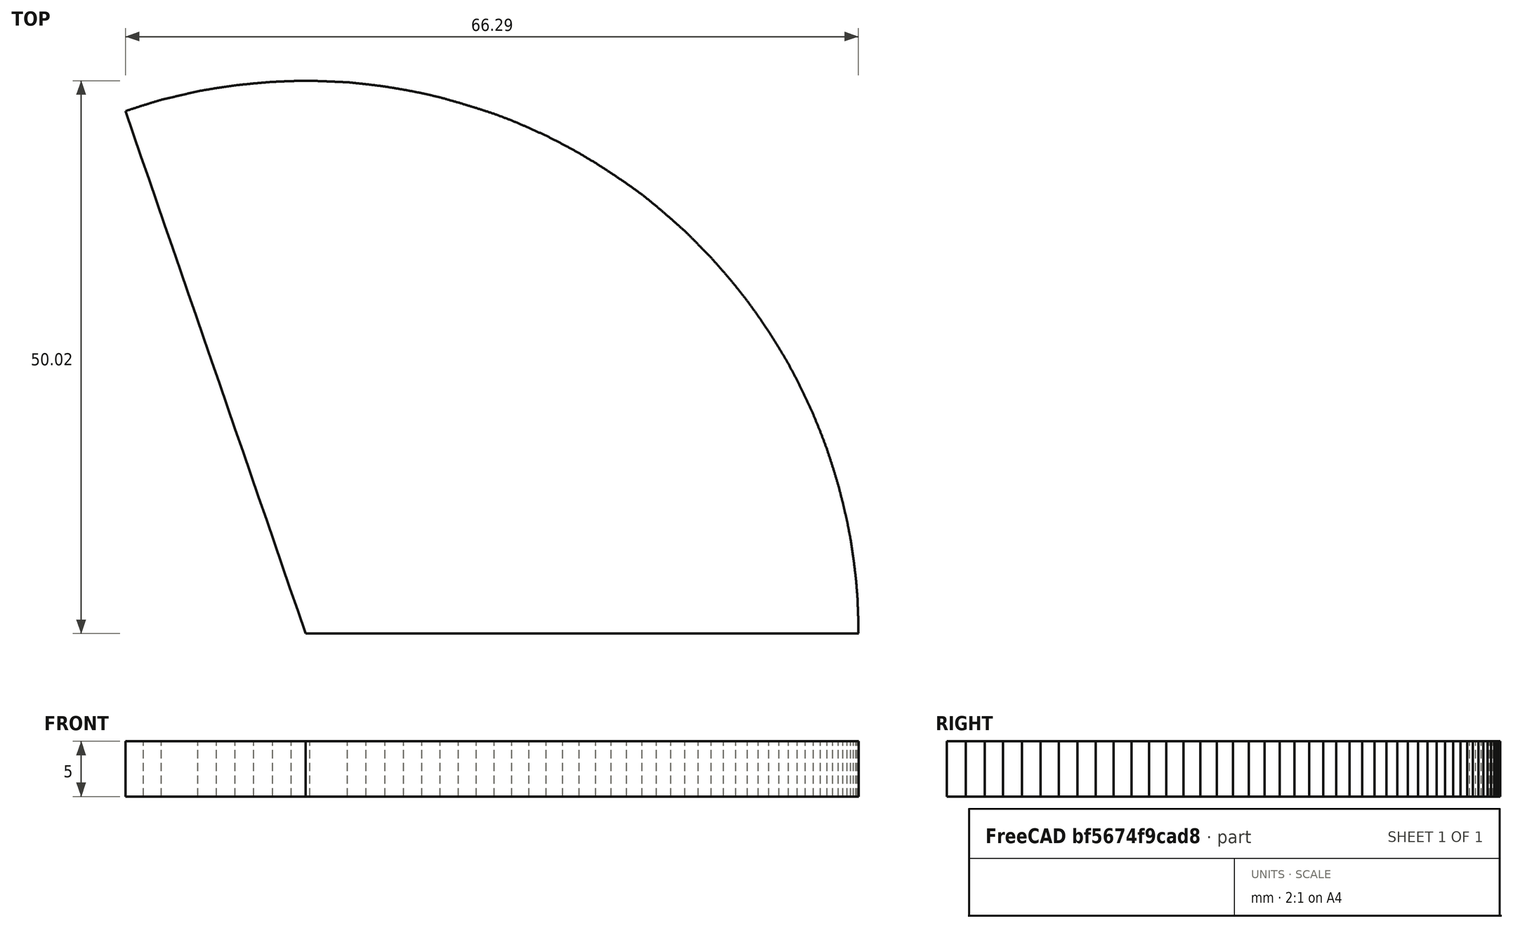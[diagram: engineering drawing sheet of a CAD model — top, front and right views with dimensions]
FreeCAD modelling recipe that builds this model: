
FCSTD DOCUMENT  (FreeCAD 0.19R)
Label: F-35_v2_parts_19
License: All rights reserved
LicenseURL: http://en.wikipedia.org/wiki/All_rights_reserved
objects: App::DocumentObjectGroup×2, PartDesign::CoordinateSystem×1, App::FeaturePython×1, Sketcher::SketchObject×1, PartDesign::Pad×1, PartDesign::Body×1, App::Part×1
note: 5 computed .brp shape members not serialized (recipe doc carries the construction recipe); baked Part::Feature solids carry a one-line shape summary decoded from their .brp

FEATURE [App::DocumentObjectGroup] Parts
FEATURE [PartDesign::CoordinateSystem] LCS_Origin
  AttacherType = Attacher::AttachEngine3D
  MapMode = 2
  Support = -> [X_Axis]
FEATURE [App::DocumentObjectGroup] Constraints
FEATURE [App::FeaturePython] Variables  # WARN: FeaturePython — macro-defined, semantics opaque (R4)
FEATURE [Sketcher::SketchObject] Sketch006
  FullyConstrained = false
  sketch-geometry (58):
    g0: BSplineCurve PolesCount=2 KnotsCount=2 Degree=1 IsPeriodic=0
    g1: BSplineCurve PolesCount=2 KnotsCount=2 Degree=1 IsPeriodic=0
    g2: BSplineCurve PolesCount=2 KnotsCount=2 Degree=1 IsPeriodic=0
    g3: BSplineCurve PolesCount=2 KnotsCount=2 Degree=1 IsPeriodic=0
    g4: BSplineCurve PolesCount=2 KnotsCount=2 Degree=1 IsPeriodic=0
    g5: BSplineCurve PolesCount=2 KnotsCount=2 Degree=1 IsPeriodic=0
    g6: BSplineCurve PolesCount=2 KnotsCount=2 Degree=1 IsPeriodic=0
    g7: BSplineCurve PolesCount=2 KnotsCount=2 Degree=1 IsPeriodic=0
    g8: BSplineCurve PolesCount=2 KnotsCount=2 Degree=1 IsPeriodic=0
    g9: BSplineCurve PolesCount=2 KnotsCount=2 Degree=1 IsPeriodic=0
    g10: BSplineCurve PolesCount=2 KnotsCount=2 Degree=1 IsPeriodic=0
    g11: BSplineCurve PolesCount=2 KnotsCount=2 Degree=1 IsPeriodic=0
    g12: BSplineCurve PolesCount=2 KnotsCount=2 Degree=1 IsPeriodic=0
    g13: BSplineCurve PolesCount=2 KnotsCount=2 Degree=1 IsPeriodic=0
    g14: BSplineCurve PolesCount=2 KnotsCount=2 Degree=1 IsPeriodic=0
    g15: BSplineCurve PolesCount=2 KnotsCount=2 Degree=1 IsPeriodic=0
    g16: BSplineCurve PolesCount=2 KnotsCount=2 Degree=1 IsPeriodic=0
    g17: BSplineCurve PolesCount=2 KnotsCount=2 Degree=1 IsPeriodic=0
    g18: BSplineCurve PolesCount=2 KnotsCount=2 Degree=1 IsPeriodic=0
    g19: BSplineCurve PolesCount=2 KnotsCount=2 Degree=1 IsPeriodic=0
    g20: BSplineCurve PolesCount=2 KnotsCount=2 Degree=1 IsPeriodic=0
    g21: BSplineCurve PolesCount=2 KnotsCount=2 Degree=1 IsPeriodic=0
    g22: BSplineCurve PolesCount=2 KnotsCount=2 Degree=1 IsPeriodic=0
    g23: BSplineCurve PolesCount=2 KnotsCount=2 Degree=1 IsPeriodic=0
    g24: BSplineCurve PolesCount=2 KnotsCount=2 Degree=1 IsPeriodic=0
    g25: BSplineCurve PolesCount=2 KnotsCount=2 Degree=1 IsPeriodic=0
    g26: BSplineCurve PolesCount=2 KnotsCount=2 Degree=1 IsPeriodic=0
    g27: BSplineCurve PolesCount=2 KnotsCount=2 Degree=1 IsPeriodic=0
    g28: BSplineCurve PolesCount=2 KnotsCount=2 Degree=1 IsPeriodic=0
    g29: BSplineCurve PolesCount=2 KnotsCount=2 Degree=1 IsPeriodic=0
    g30: BSplineCurve PolesCount=2 KnotsCount=2 Degree=1 IsPeriodic=0
    g31: BSplineCurve PolesCount=2 KnotsCount=2 Degree=1 IsPeriodic=0
    g32: BSplineCurve PolesCount=2 KnotsCount=2 Degree=1 IsPeriodic=0
    g33: BSplineCurve PolesCount=2 KnotsCount=2 Degree=1 IsPeriodic=0
    g34: BSplineCurve PolesCount=2 KnotsCount=2 Degree=1 IsPeriodic=0
    g35: BSplineCurve PolesCount=2 KnotsCount=2 Degree=1 IsPeriodic=0
    g36: BSplineCurve PolesCount=2 KnotsCount=2 Degree=1 IsPeriodic=0
    g37: BSplineCurve PolesCount=2 KnotsCount=2 Degree=1 IsPeriodic=0
    g38: BSplineCurve PolesCount=2 KnotsCount=2 Degree=1 IsPeriodic=0
    g39: BSplineCurve PolesCount=2 KnotsCount=2 Degree=1 IsPeriodic=0
    g40: BSplineCurve PolesCount=2 KnotsCount=2 Degree=1 IsPeriodic=0
    g41: BSplineCurve PolesCount=2 KnotsCount=2 Degree=1 IsPeriodic=0
    g42: BSplineCurve PolesCount=2 KnotsCount=2 Degree=1 IsPeriodic=0
    g43: BSplineCurve PolesCount=2 KnotsCount=2 Degree=1 IsPeriodic=0
    g44: BSplineCurve PolesCount=2 KnotsCount=2 Degree=1 IsPeriodic=0
    g45: BSplineCurve PolesCount=2 KnotsCount=2 Degree=1 IsPeriodic=0
    g46: BSplineCurve PolesCount=2 KnotsCount=2 Degree=1 IsPeriodic=0
    g47: BSplineCurve PolesCount=2 KnotsCount=2 Degree=1 IsPeriodic=0
    g48: BSplineCurve PolesCount=2 KnotsCount=2 Degree=1 IsPeriodic=0
    g49: BSplineCurve PolesCount=2 KnotsCount=2 Degree=1 IsPeriodic=0
    g50: BSplineCurve PolesCount=2 KnotsCount=2 Degree=1 IsPeriodic=0
    g51: BSplineCurve PolesCount=2 KnotsCount=2 Degree=1 IsPeriodic=0
    g52: BSplineCurve PolesCount=2 KnotsCount=2 Degree=1 IsPeriodic=0
    g53: BSplineCurve PolesCount=2 KnotsCount=2 Degree=1 IsPeriodic=0
    g54: BSplineCurve PolesCount=2 KnotsCount=2 Degree=1 IsPeriodic=0
    g55: BSplineCurve PolesCount=2 KnotsCount=2 Degree=1 IsPeriodic=0
    g56: BSplineCurve PolesCount=2 KnotsCount=2 Degree=1 IsPeriodic=0
    g57: BSplineCurve PolesCount=2 KnotsCount=2 Degree=1 IsPeriodic=0
  constraints (55):
    c: Coincident(g2,g3)
    c: Coincident(g3,g4)
    c: Coincident(g4,g5)
    c: Coincident(g5,g6)
    c: Coincident(g6,g7)
    c: Coincident(g7,g8)
    c: Coincident(g8,g9)
    c: Coincident(g9,g10)
    c: Coincident(g10,g11)
    c: Coincident(g11,g12)
    c: Coincident(g12,g13)
    c: Coincident(g13,g14)
    c: Coincident(g14,g15)
    c: Coincident(g15,g16)
    c: Coincident(g16,g17)
    c: Coincident(g17,g18)
    c: Coincident(g18,g19)
    c: Coincident(g19,g20)
    c: Coincident(g20,g21)
    c: Coincident(g21,g22)
    c: Coincident(g22,g23)
    c: Coincident(g23,g24)
    c: Coincident(g24,g25)
    c: Coincident(g25,g26)
    c: Coincident(g26,g27)
    c: Coincident(g27,g28)
    c: Coincident(g28,g29)
    c: Coincident(g29,g30)
    c: Coincident(g30,g31)
    c: Coincident(g31,g32)
    c: Coincident(g32,g33)
    c: Coincident(g33,g34)
    c: Coincident(g34,g35)
    c: Coincident(g35,g36)
    c: Coincident(g36,g37)
    c: Coincident(g37,g38)
    c: Coincident(g38,g39)
    c: Coincident(g39,g40)
    c: Coincident(g40,g41)
    c: Coincident(g41,g42)
    c: Coincident(g42,g43)
    c: Coincident(g43,g44)
    c: Coincident(g44,g45)
    c: Coincident(g45,g46)
    c: Coincident(g46,g47)
    c: Coincident(g47,g48)
    c: Coincident(g48,g49)
    c: Coincident(g49,g50)
    c: Coincident(g50,g51)
    c: Coincident(g51,g52)
    c: Coincident(g52,g53)
    c: Coincident(g53,g54)
    c: Coincident(g54,g55)
    c: Coincident(g55,g56)
    c: Coincident(g56,g57)
FEATURE [PartDesign::Pad] Pad
  Direction = (1,1,1)
  Length = 5
  Length2 = 100
  Profile = -> Sketch006
  Type = 0
FEATURE [PartDesign::Body] Body006  label="Part19"
  Group = -> [Sketch006,Pad]
  Origin = -> Origin007
  Tip = -> Pad
FEATURE [App::Part] Model
  Configuration = 0
  Group = -> [LCS_Origin,Constraints,Variables,Body006]
  Origin = -> Origin
  Type = Assembly4 Model
